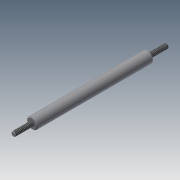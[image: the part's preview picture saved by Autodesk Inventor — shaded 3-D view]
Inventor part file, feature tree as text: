
AUTODESK INVENTOR PART (.ipt)
format: ipt  version: 2013 (Build 170138000, 138)  size: 97,280 bytes
history: native  units: mm
features: sketch x6, extrude x3, chamfer x3, hole x2, thread x2
ambient origin geometry x8: Origin, YZ Plane, XZ Plane, XY Plane, X Axis, Y Axis, Z Axis, Center Point
bodies: Solid1 (feature_tree)
feature tree (16):
  extrude  "Extrusion1"  Depth=62.7mm TaperAngle=0.0deg
  hole  "Hole1"  [1 undecoded]
  hole  "Hole2"  [1 undecoded]
  chamfer  "Chamfer1"  Distance=10.0mm
  extrude  "Extrusion2"  Depth=10.0mm TaperAngle=0.0deg
  extrude  "Extrusion3"  [1 undecoded]
  sketch  "Sketch6"  dims[d31=0.3mm d32=2.0mm d33=45.0deg]
  thread  "Thread1"  [1 undecoded]
  chamfer  "Chamfer2"  [1 undecoded]
  thread  "Thread2"  [1 undecoded]
  chamfer  "Chamfer3"  [1 undecoded]
  sketch  "Sketch1"  dims[d0=6.0mm d1=62.7mm d2=0.0mm]
  sketch  "Sketch2"  dims[d3=2.459mm d4=6.0mm d5=4.0mm d6=2.0mm d7=90.0deg d8=8.0mm d9=0.0mm]
  sketch  "Sketch3"  dims[d10=2.459mm d11=6.0mm d12=4.0mm d13=2.0mm d14=90.0deg d15=8.0mm d16=0.0mm d17=0.5mm d18=2.0mm d19=45.0deg]
  sketch  "Sketch4"  dims[d20=10.0mm d21=0.0mm d22=10.0mm d23=0.0mm d24=10.0mm d25=0.0mm]
  sketch  "Sketch5"  dims[d26=0.3mm d27=2.0mm d28=45.0deg d29=10.0mm d30=0.0mm]
note: 7 required parameter values undecoded (feature->parameter linkage not recoverable at this tier; creation-order binding heuristic only, values carry confidence <= 0.55)
